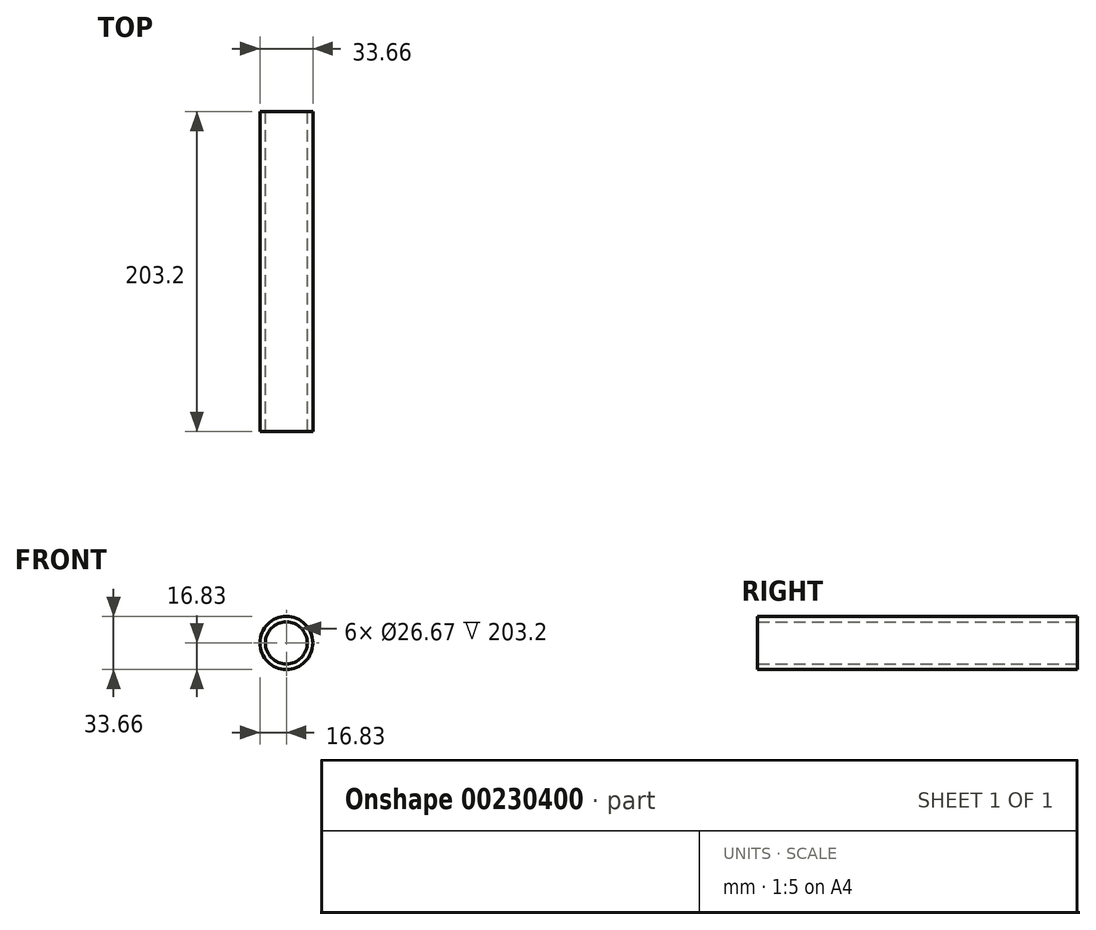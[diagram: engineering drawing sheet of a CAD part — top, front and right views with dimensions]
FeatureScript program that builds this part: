
annotation { "Feature Type Name" : "Feature", "Feature Type Description" : "" }
export const myFeature = defineFeature(function(context is Context, id is Id, definition is map)
    precondition{}
    {
        {
            var Q0;
            Q0=qCreatedBy(makeId("Front.planeOp"),FACE);
            var sketch = newSketch(context, id + "F0", { "sketchPlane" : qUnion([Q0])});
            skCircle(sketch, "E0", {"center": v(0, 0) * mm, "radius": 13.34 * mm});
            skCircle(sketch, "E1", {"center": v(0, 0) * mm, "radius": 16.83 * mm});
            skSolve(sketch);
        }
        {
            var Q0;
            Q0 = qSketchRegion(id + "F0", true);
            extrude(context, id + "F1", {"entities" : qUnion([Q0]), "depth" : 203.2 * mm});
        }
    });
